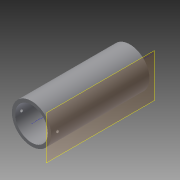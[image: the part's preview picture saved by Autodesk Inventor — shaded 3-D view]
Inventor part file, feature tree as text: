
AUTODESK INVENTOR PART (.ipt)
format: ipt  version: 2015 SP2 (Build 190223200, 223)  size: 99,840 bytes
history: native  units: mm
features: sketch x3, extrude x1, plane x1, hole x1
ambient origin geometry x8: Origin, YZ Plane, XZ Plane, XY Plane, X Axis, Y Axis, Z Axis, Center Point
bodies: Solid1 (feature_tree)
feature tree (6):
  extrude  "Extrusion1"  Depth=30.0mm
  plane  "Work Plane1"
  hole  "Hole1"  [1 undecoded]
  sketch  "Sketch3"
  sketch  "Sketch1"  dims[d2=150.0mm d3=0.0mm d4=30.0mm]
  sketch  "Sketch2"  dims[d7=4.5mm d8=6.0mm d9=4.0mm d10=2.0mm d11=90.0deg d12=8.0mm d13=20.594885mm]
note: 1 required parameter value undecoded (feature->parameter linkage not recoverable at this tier; creation-order binding heuristic only, values carry confidence <= 0.55)
